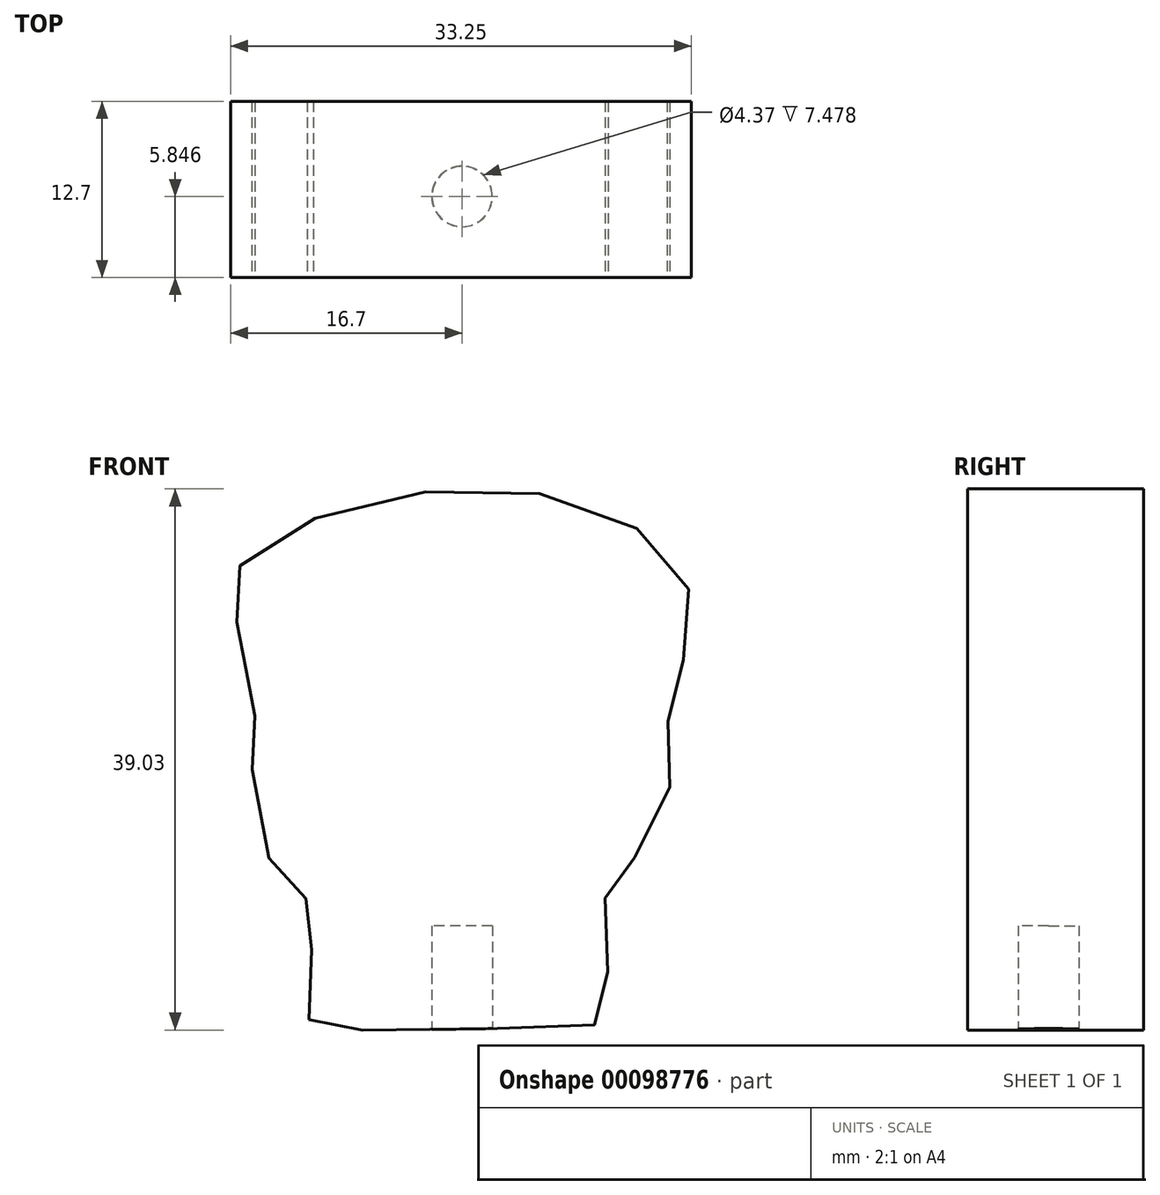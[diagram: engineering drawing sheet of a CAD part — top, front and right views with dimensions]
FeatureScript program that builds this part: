
annotation { "Feature Type Name" : "Feature", "Feature Type Description" : "" }
export const myFeature = defineFeature(function(context is Context, id is Id, definition is map)
    precondition{}
    {
        {
            var Q0;
            Q0=qCreatedBy(makeId("Front.planeOp"),FACE);
            var sketch = newSketch(context, id + "F0", { "sketchPlane" : qUnion([Q0])});
            skFitSpline(sketch, "E0", {"points": [v(-11.05, 5.92) * mm, v(-10.75, 12.2) * mm, v(-11.31, 14.72) * mm, v(-13.93, 17.58) * mm, v(-15.1, 26.48) * mm, v(-14.95, 28.1) * mm, v(-15.56, 31.06) * mm, v(-16.03, 33.82) * mm, v(-16.54, 37.76) * mm, v(-8.14, 42.9) * mm, v(7.91, 43.36) * mm, v(16.12, 37.67) * mm, v(15.84, 31.42) * mm, v(14.8, 26.62) * mm, v(14.5, 20.63) * mm, v(10.42, 15.25) * mm, v(10.42, 14.25) * mm, v(10.22, 6.27) * mm, v(8.92, 5.48) * mm, v(-8.93, 5.18) * mm, v(-11.05, 5.92) * mm]});
            skSolve(sketch);
        }
        {
            var Q0;
            Q0 = qSketchRegion(id + "F0", true);
            extrude(context, id + "F1", {"entities" : qUnion([Q0]), "depth" : 12.7 * mm});
        }
        {
            var Q0;
            Q0=qCreatedBy(makeId("Top.planeOp"),FACE);
            var sketch = newSketch(context, id + "F2", { "sketchPlane" : qUnion([Q0])});
            skCircle(sketch, "E1", {"center": v(0, -6.85) * mm, "radius": 2.18 * mm});
            skSolve(sketch);
        }
        {
            var Q0;
            Q0 = qSketchRegion(id + "F2", true);
            extrude(context, id + "F3", {"entities" : qUnion([Q0]), "operationType" : NewBodyOperationType.REMOVE, "depth" : 12.7 * mm});
        }
    });
